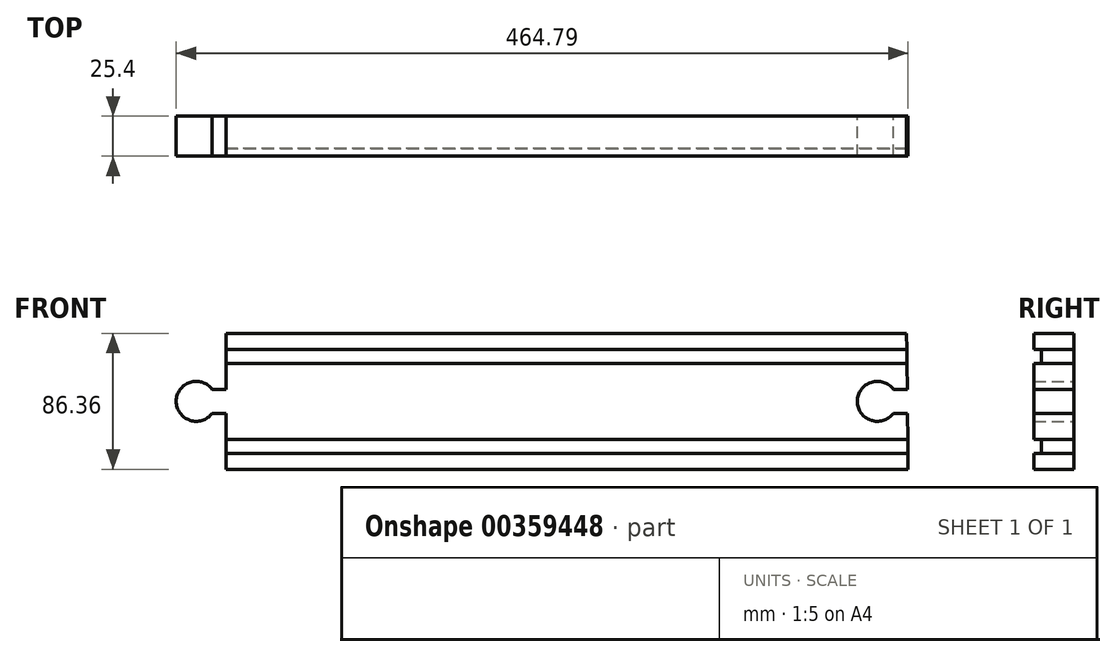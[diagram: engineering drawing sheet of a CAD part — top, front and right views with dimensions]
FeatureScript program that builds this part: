
annotation { "Feature Type Name" : "Feature", "Feature Type Description" : "" }
export const myFeature = defineFeature(function(context is Context, id is Id, definition is map)
    precondition{}
    {
        {
            var Q0;
            Q0=qCreatedBy(makeId("Front.planeOp"),FACE);
            var sketch = newSketch(context, id + "F0", { "sketchPlane" : qUnion([Q0])});
            skLineSegment(sketch, "E0", {"start": v(-188.83, 58.02) * mm, "end": v(243.35, 58.02) * mm});
            skLineSegment(sketch, "E1", {"start": v(244.21, -28.34) * mm, "end": v(-188.83, -28.34) * mm});
            skLineSegment(sketch, "E2", {"start": v(-188.83, -28.34) * mm, "end": v(-188.83, 58.02) * mm});
            skLineSegment(sketch, "E3", {"start": v(243.35, 58.02) * mm, "end": v(244.21, -28.34) * mm});
            skLineSegment(sketch, "E4", {"start": v(-188.83, 47.86) * mm, "end": v(243.45, 47.86) * mm});
            skLineSegment(sketch, "E5", {"start": v(243.54, 38.97) * mm, "end": v(-188.83, 38.97) * mm});
            skLineSegment(sketch, "E6", {"start": v(-188.83, -18.18) * mm, "end": v(244.11, -18.18) * mm});
            skLineSegment(sketch, "E7", {"start": v(244.02, -9.3) * mm, "end": v(-188.83, -9.3) * mm});
            skLineSegment(sketch, "E8", {"start": v(243.7, 22.46) * mm, "end": v(234.81, 22.37) * mm});
            skLineSegment(sketch, "E9", {"start": v(243.86, 7.22) * mm, "end": v(234.81, 7.13) * mm});
            skCircle(sketch, "E10", {"center": v(224.72, 14.84) * mm, "radius": 12.7 * mm});
            skPoint(sketch, "E10.centerSnap0", {"position": v(243.78, 14.84) * mm});
            skLineSegment(sketch, "E11", {"start": v(-188.83, 22.46) * mm, "end": v(-197.72, 22.46) * mm});
            skLineSegment(sketch, "E12", {"start": v(-188.83, 7.22) * mm, "end": v(-197.72, 7.22) * mm});
            skCircle(sketch, "E13", {"center": v(-207.88, 14.84) * mm, "radius": 12.7 * mm});
            skPoint(sketch, "E13.centerSnap0", {"position": v(-188.83, 14.84) * mm});
            skSolve(sketch);
        }
        {
            var Q0;
            {var subQ0=sQuery(id+"F0.wireOp",EDGE,"E5");Q0=makeQuery(id+"F0.imprint","IMPRINT",FACE,{"disambiguationData":[TD([[makeQuery(id+"F0.imprint","IMPRINT",EDGE,{"derivedFrom":subQ0}),1.0]])]});}
            var Q1;
            {var subQ0=sQuery(id+"F0.wireOp",EDGE,"E1");Q1=makeQuery(id+"F0.imprint","IMPRINT",FACE,{"disambiguationData":[TD([[makeQuery(id+"F0.imprint","IMPRINT",EDGE,{"derivedFrom":subQ0}),-1.0]])]});}
            var Q2;
            {var subQ0=sQuery(id+"F0.wireOp",EDGE,"E13");var subQ1=makeQuery(id+"F0.imprint","INTERSECT",VERTEX,{"derivedFrom":[sQuery(id+"F0.wireOp",EDGE,"E12"),subQ0]});Q2=makeQuery(id+"F0.imprint","IMPRINT",FACE,{"disambiguationData":[TD([[makeQuery(id+"F0.imprint","IMPRINT",EDGE,{"disambiguationData":[TD([[subQ1,1.0]])],"derivedFrom":subQ0}),1.0]])]});}
            var Q3;
            {var subQ3=sQuery(id+"F0.wireOp",EDGE,"E12");Q3=makeQuery(id+"F0.imprint","IMPRINT",FACE,{"disambiguationData":[TD([[makeQuery(id+"F0.imprint","IMPRINT",EDGE,{"derivedFrom":subQ3}),-1.0]])]});}
            var Q4;
            {var subQ0=sQuery(id+"F0.wireOp",EDGE,"E0");Q4=makeQuery(id+"F0.imprint","IMPRINT",FACE,{"disambiguationData":[TD([[makeQuery(id+"F0.imprint","IMPRINT",EDGE,{"derivedFrom":subQ0}),-1.0]])]});}
            extrude(context, id + "F1", {"entities" : qUnion([Q0, Q1, Q2, Q3, Q4]), "depth" : 25.4 * mm});
        }
        {
            var Q0;
            {var subQ0=sQuery(id+"F0.wireOp",EDGE,"E4");Q0=makeQuery(id+"F0.imprint","IMPRINT",FACE,{"disambiguationData":[TD([[makeQuery(id+"F0.imprint","IMPRINT",EDGE,{"derivedFrom":subQ0}),-1.0]])]});}
            var Q1;
            {var subQ0=sQuery(id+"F0.wireOp",EDGE,"E6");Q1=makeQuery(id+"F0.imprint","IMPRINT",FACE,{"disambiguationData":[TD([[makeQuery(id+"F0.imprint","IMPRINT",EDGE,{"derivedFrom":subQ0}),1.0]])]});}
            extrude(context, id + "F2", {"entities" : qUnion([Q0, Q1]), "depth" : 20.64 * mm});
        }
    });
